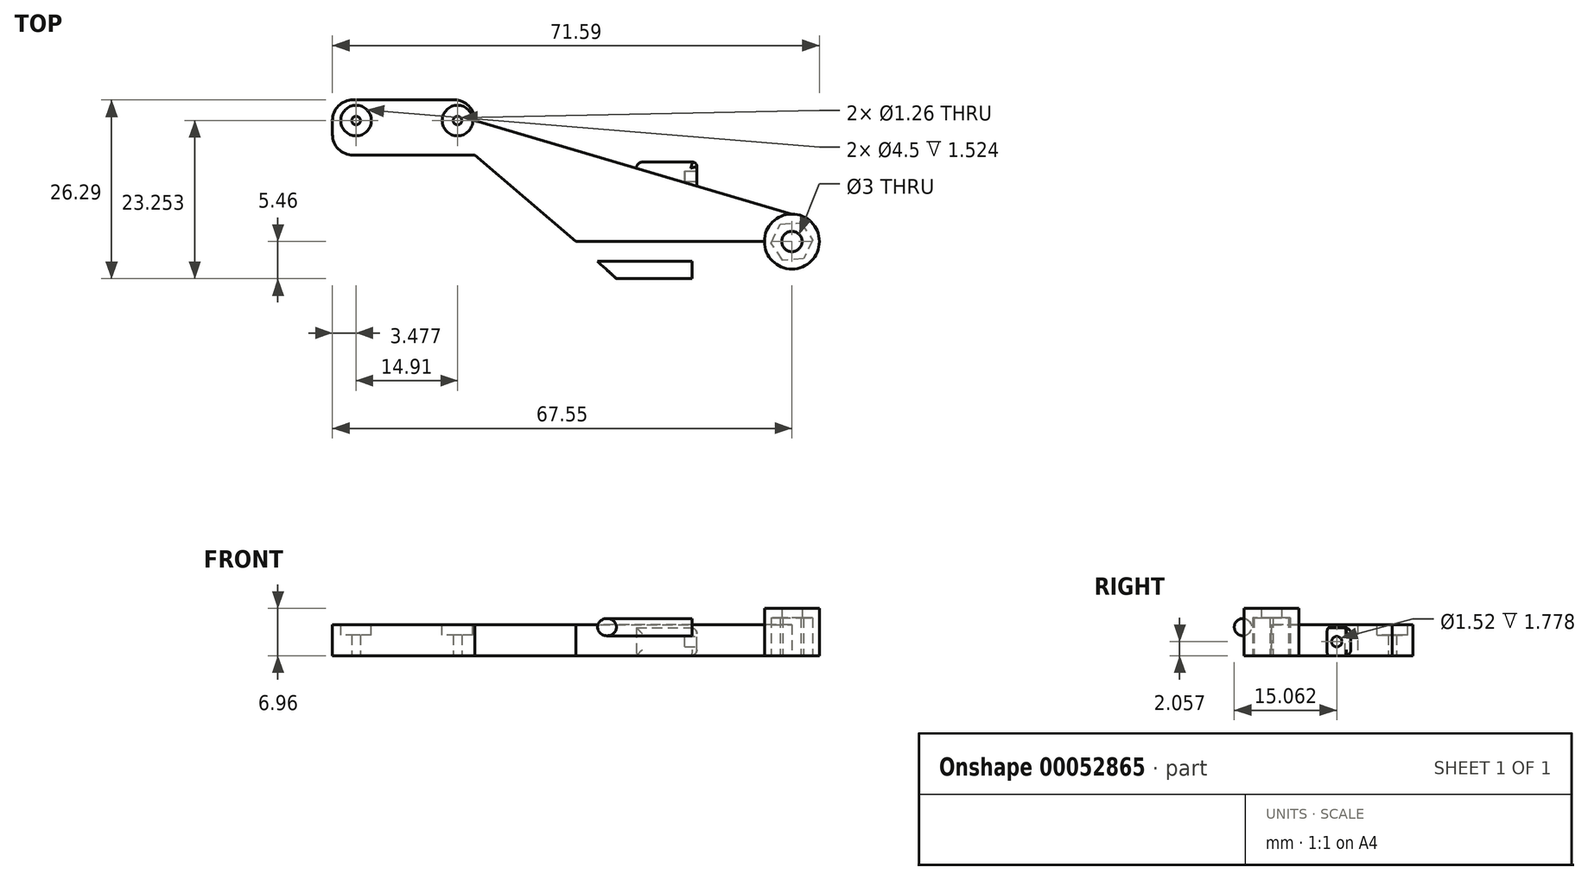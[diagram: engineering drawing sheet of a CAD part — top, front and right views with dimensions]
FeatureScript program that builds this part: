
annotation { "Feature Type Name" : "Feature", "Feature Type Description" : "" }
export const myFeature = defineFeature(function(context is Context, id is Id, definition is map)
    precondition{}
    {
        {
            var Q0;
            Q0=qCreatedBy(makeId("Top.planeOp"),FACE);
            var sketch = newSketch(context, id + "F0", { "sketchPlane" : qUnion([Q0])});
            skLineSegment(sketch, "E0", {"start": v(0, 0) * mm, "end": v(-31.75, 0) * mm});
            skLineSegment(sketch, "E1", {"start": v(-31.75, 0) * mm, "end": v(-46.62, 12.7) * mm});
            skLineSegment(sketch, "E2", {"start": v(-46.62, 12.7) * mm, "end": v(0, 0) * mm});
            skLineSegment(sketch, "E3", {"start": v(0, 0) * mm, "end": v(0, 4.04) * mm});
            skCircle(sketch, "E4", {"center": v(0, 0) * mm, "radius": 4.04 * mm});
            skLineSegment(sketch, "E5.bottom", {"start": v(-46.62, 12.7) * mm, "end": v(-64.5, 12.7) * mm});
            skLineSegment(sketch, "E5.top", {"start": v(-49.67, 20.83) * mm, "end": v(-64.5, 20.83) * mm});
            skLineSegment(sketch, "E5.left", {"start": v(-46.62, 12.7) * mm, "end": v(-46.62, 17.78) * mm});
            skLineSegment(sketch, "E5.right", {"start": v(-67.55, 15.75) * mm, "end": v(-67.55, 17.78) * mm});
            skCircle(sketch, "E6", {"center": v(-49.16, 17.8) * mm, "radius": 0.63 * mm});
            skCircle(sketch, "E7", {"center": v(-64.07, 17.8) * mm, "radius": 0.63 * mm});
            skPoint(sketch, "E8.visualSharp", {"position": v(-67.55, 20.83) * mm});
            skArc(sketch, "E8.filletArc", {"start": v(-64.5, 20.83) * mm, "mid": v(-66.66, 19.94) * mm, "end": v(-67.55, 17.78) * mm});
            skPoint(sketch, "E9.visualSharp", {"position": v(-67.55, 12.7) * mm});
            skArc(sketch, "E9.filletArc", {"start": v(-67.55, 15.75) * mm, "mid": v(-66.66, 13.6) * mm, "end": v(-64.5, 12.7) * mm});
            skPoint(sketch, "E10.visualSharp", {"position": v(-46.62, 20.83) * mm});
            skArc(sketch, "E10.filletArc", {"start": v(-46.62, 17.78) * mm, "mid": v(-47.52, 19.94) * mm, "end": v(-49.67, 20.83) * mm});
            skLineSegment(sketch, "E11", {"start": v(-46.62, 17.78) * mm, "end": v(0, 4.04) * mm});
            skLineSegment(sketch, "E12", {"start": v(-46.62, 12.7) * mm, "end": v(-49.67, 12.7) * mm});
            skLineSegment(sketch, "E13", {"start": v(-46.62, 12.7) * mm, "end": v(-44.3, 10.72) * mm});
            skLineSegment(sketch, "E14", {"start": v(-49.67, 12.7) * mm, "end": v(-44.3, 10.72) * mm});
            skCircle(sketch, "E15", {"center": v(0, 0) * mm, "radius": 1.5 * mm});
            skLineSegment(sketch, "E16", {"start": v(-44.3, 10.72) * mm, "end": v(-20.3, -9.78) * mm});
            skLineSegment(sketch, "E17", {"start": v(-21, -9.17) * mm, "end": v(-44.3, 10.72) * mm});
            skLineSegment(sketch, "E18", {"start": v(-31.75, 0) * mm, "end": v(-22.66, 0) * mm});
            skLineSegment(sketch, "E19", {"start": v(-22.66, 0) * mm, "end": v(-22.66, -4.18) * mm});
            skLineSegment(sketch, "E20", {"start": v(-22.66, 0) * mm, "end": v(-21.74, -2.29) * mm});
            skSolve(sketch);
        }
        {
            var Q0;
            Q0=makeQuery(id+"F0.imprint","IMPRINT",FACE,{"disambiguationData":[TD([[makeQuery(id+"F0.imprint","IMPRINT",EDGE,{"derivedFrom":sQuery(id+"F0.wireOp",EDGE,"E5.bottom")}),-1.0]])]});
            var Q1;
            Q1=makeQuery(id+"F0.imprint","IMPRINT",FACE,{"disambiguationData":[TD([[makeQuery(id+"F0.imprint","IMPRINT",EDGE,{"derivedFrom":sQuery(id+"F0.wireOp",EDGE,"E12")}),1.0]])]});
            var Q2;
            {var subQ0=sQuery(id+"F0.wireOp",EDGE,"E5.left");Q2=makeQuery(id+"F0.imprint","IMPRINT",FACE,{"disambiguationData":[TD([[makeQuery(id+"F0.imprint","IMPRINT",EDGE,{"derivedFrom":subQ0}),-1.0]])]});}
            var Q3;
            {var subQ5=sQuery(id+"F0.wireOp",EDGE,"E1");Q3=makeQuery(id+"F0.imprint","IMPRINT",FACE,{"disambiguationData":[TD([[makeQuery(id+"F0.imprint","IMPRINT",EDGE,{"derivedFrom":subQ5}),-1.0]])]});}
            var Q4;
            {var subQ0=sQuery(id+"F0.wireOp",EDGE,"E4");var subQ1=sQuery(id+"F0.wireOp",EDGE,"E2");var subQ2=makeQuery(id+"F0.imprint","INTERSECT",VERTEX,{"derivedFrom":[subQ1,subQ0]});Q4=makeQuery(id+"F0.imprint","IMPRINT",FACE,{"disambiguationData":[TD([[makeQuery(id+"F0.imprint","IMPRINT",EDGE,{"disambiguationData":[TD([[subQ2,-1.0]])],"derivedFrom":subQ1}),1.0]])]});}
            var Q5;
            {var subQ0=sQuery(id+"F0.wireOp",EDGE,"E4");var subQ1=sQuery(id+"F0.wireOp",EDGE,"E0");var subQ2=makeQuery(id+"F0.imprint","INTERSECT",VERTEX,{"derivedFrom":[subQ1,subQ0]});Q5=makeQuery(id+"F0.imprint","IMPRINT",FACE,{"disambiguationData":[TD([[makeQuery(id+"F0.imprint","IMPRINT",EDGE,{"disambiguationData":[TD([[subQ2,1.0]])],"derivedFrom":subQ1}),-1.0]])]});}
            var Q6;
            {var subQ0=sQuery(id+"F0.wireOp",EDGE,"E4");var subQ1=sQuery(id+"F0.wireOp",EDGE,"E0");var subQ2=makeQuery(id+"F0.imprint","INTERSECT",VERTEX,{"derivedFrom":[subQ1,subQ0]});Q6=makeQuery(id+"F0.imprint","IMPRINT",FACE,{"disambiguationData":[TD([[makeQuery(id+"F0.imprint","IMPRINT",EDGE,{"disambiguationData":[TD([[subQ2,1.0]])],"derivedFrom":subQ1}),1.0]])]});}
            var Q7;
            {var subQ0=sQuery(id+"F0.wireOp",EDGE,"E13");Q7=makeQuery(id+"F0.imprint","IMPRINT",FACE,{"disambiguationData":[TD([[makeQuery(id+"F0.imprint","IMPRINT",EDGE,{"derivedFrom":subQ0}),1.0]])]});}
            extrude(context, id + "F1", {"entities" : qUnion([Q0, Q1, Q2, Q3, Q4, Q5, Q6, Q7]), "depth" : 4.57 * mm});
        }
        {
            var Q0;
            {var subQ0=sQuery(id+"F0.wireOp",EDGE,"E4");var subQ1=sQuery(id+"F0.wireOp",EDGE,"E2");var subQ2=makeQuery(id+"F0.imprint","INTERSECT",VERTEX,{"derivedFrom":[subQ1,subQ0]});Q0=makeQuery(id+"F0.imprint","IMPRINT",FACE,{"disambiguationData":[TD([[makeQuery(id+"F0.imprint","IMPRINT",EDGE,{"disambiguationData":[TD([[subQ2,-1.0]])],"derivedFrom":subQ1}),1.0]])]});}
            var Q1;
            {var subQ0=sQuery(id+"F0.wireOp",EDGE,"E4");var subQ1=sQuery(id+"F0.wireOp",EDGE,"E0");var subQ2=makeQuery(id+"F0.imprint","INTERSECT",VERTEX,{"derivedFrom":[subQ1,subQ0]});Q1=makeQuery(id+"F0.imprint","IMPRINT",FACE,{"disambiguationData":[TD([[makeQuery(id+"F0.imprint","IMPRINT",EDGE,{"disambiguationData":[TD([[subQ2,1.0]])],"derivedFrom":subQ1}),1.0]])]});}
            var Q2;
            {var subQ0=sQuery(id+"F0.wireOp",EDGE,"E4");var subQ1=sQuery(id+"F0.wireOp",EDGE,"E0");var subQ2=makeQuery(id+"F0.imprint","INTERSECT",VERTEX,{"derivedFrom":[subQ1,subQ0]});Q2=makeQuery(id+"F0.imprint","IMPRINT",FACE,{"disambiguationData":[TD([[makeQuery(id+"F0.imprint","IMPRINT",EDGE,{"disambiguationData":[TD([[subQ2,1.0]])],"derivedFrom":subQ1}),-1.0]])]});}
            extrude(context, id + "F2", {"entities" : qUnion([Q0, Q1, Q2]), "operationType" : NewBodyOperationType.ADD, "depth" : 6.96 * mm});
        }
        {
            var Q0;
            Q0=makeQuery(id+"F1.opExtrude","CAP_FACE",FACE,{"disambiguationData":[OSD([sQuery(id+"F0.wireOp",EDGE,"E0"),sQuery(id+"F0.wireOp",EDGE,"E1"),sQuery(id+"F0.wireOp",EDGE,"E4"),sQuery(id+"F0.wireOp",EDGE,"E5.bottom"),sQuery(id+"F0.wireOp",EDGE,"E5.top"),sQuery(id+"F0.wireOp",EDGE,"E5.right"),sQuery(id+"F0.wireOp",EDGE,"E6"),sQuery(id+"F0.wireOp",EDGE,"E7"),sQuery(id+"F0.wireOp",EDGE,"E8.filletArc"),sQuery(id+"F0.wireOp",EDGE,"E9.filletArc"),sQuery(id+"F0.wireOp",EDGE,"E10.filletArc"),sQuery(id+"F0.wireOp",EDGE,"E11"),sQuery(id+"F0.wireOp",EDGE,"E14"),sQuery(id+"F0.wireOp",EDGE,"E15")])],"isStart":false});
            var sketch = newSketch(context, id + "F3", { "sketchPlane" : qUnion([Q0])});
            skCircle(sketch, "E21", {"center": v(-64.07, 17.8) * mm, "radius": 2.25 * mm});
            skCircle(sketch, "E22", {"center": v(-49.16, 17.8) * mm, "radius": 1.35 * mm});
            skCircle(sketch, "E23", {"center": v(-49.16, 17.8) * mm, "radius": 2.25 * mm});
            skSolve(sketch);
        }
        {
            var Q0;
            Q0=makeQuery(id+"F3.imprint","IMPRINT",FACE,{"disambiguationData":[TD([[makeQuery(id+"F3.imprint","IMPRINT",EDGE,{"derivedFrom":sQuery(id+"F3.wireOp",EDGE,"E21")}),1.0]])]});
            var Q1;
            Q1=makeQuery(id+"F3.imprint","IMPRINT",FACE,{"disambiguationData":[TD([[makeQuery(id+"F3.imprint","IMPRINT",EDGE,{"derivedFrom":sQuery(id+"F3.wireOp",EDGE,"E22")}),-1.0]])]});
            var Q2;
            Q2=makeQuery(id+"F3.imprint","IMPRINT",FACE,{"disambiguationData":[TD([[makeQuery(id+"F3.imprint","IMPRINT",EDGE,{"derivedFrom":sQuery(id+"F3.wireOp",EDGE,"E22")}),1.0]])]});
            extrude(context, id + "F4", {"entities" : qUnion([Q0, Q1, Q2]), "operationType" : NewBodyOperationType.REMOVE, "oppositeDirection" : true, "depth" : 1.52 * mm});
        }
        {
            var Q0;
            Q0=qCreatedBy(makeId("Top.planeOp"),FACE);
            var sketch = newSketch(context, id + "F5", { "sketchPlane" : qUnion([Q0])});
            skLineSegment(sketch, "E24", {"start": v(0, 0) * mm, "end": v(-14.7, 0) * mm});
            skLineSegment(sketch, "E25", {"start": v(-14.7, 0) * mm, "end": v(-14.7, -8.38) * mm});
            skLineSegment(sketch, "E26", {"start": v(-14.7, 0) * mm, "end": v(-31.75, 0) * mm});
            skLineSegment(sketch, "E27", {"start": v(-14.7, -8.38) * mm, "end": v(-22.62, -8.38) * mm});
            skLineSegment(sketch, "E28", {"start": v(-22.62, -8.38) * mm, "end": v(-31.75, 0) * mm});
            skLineSegment(sketch, "E29", {"start": v(-14.6, 11.68) * mm, "end": v(-22.86, 11.68) * mm});
            skLineSegment(sketch, "E30", {"start": v(-22.86, 11.68) * mm, "end": v(-22.86, 4.7) * mm});
            skLineSegment(sketch, "E31", {"start": v(-22.86, 4.7) * mm, "end": v(-13.97, 4.7) * mm});
            skLineSegment(sketch, "E32", {"start": v(-13.97, 4.7) * mm, "end": v(-13.97, 11.05) * mm});
            skPoint(sketch, "E33.visualSharp", {"position": v(-13.97, 11.68) * mm});
            skArc(sketch, "E33.filletArc", {"start": v(-13.97, 11.05) * mm, "mid": v(-14.16, 11.5) * mm, "end": v(-14.6, 11.68) * mm});
            skSolve(sketch);
        }
        {
            var Q0;
            Q0=makeQuery(id+"F5.imprint","IMPRINT",FACE,{"disambiguationData":[TD([[makeQuery(id+"F5.imprint","IMPRINT",EDGE,{"derivedFrom":sQuery(id+"F5.wireOp",EDGE,"E29")}),1.0]])]});
            extrude(context, id + "F6", {"entities" : qUnion([Q0]), "operationType" : NewBodyOperationType.ADD, "depth" : 4.11 * mm});
        }
        {
            var Q0;
            Q0=makeQuery(id+"F5.imprint","IMPRINT",FACE,{"disambiguationData":[TD([[makeQuery(id+"F5.imprint","IMPRINT",EDGE,{"derivedFrom":sQuery(id+"F5.wireOp",EDGE,"E25")}),-1.0]])]});
            extrude(context, id + "F7", {"entities" : qUnion([Q0]), "operationType" : NewBodyOperationType.ADD, "depth" : 8.38 * mm});
        }
        {
            var Q0;
            Q0=makeQuery(id+"F7.opExtrude","CAP_EDGE",EDGE,{"disambiguationData":[OSD([sQuery(id+"F5.wireOp",EDGE,"E26")])],"isStart":false});
            var Q1;
            Q1=makeQuery(id+"F7.opExtrude","CAP_EDGE",EDGE,{"disambiguationData":[OSD([sQuery(id+"F5.wireOp",EDGE,"E27")])],"isStart":false});
            var Q2;
            Q2=makeQuery(id+"F7.opExtrude","CAP_EDGE",EDGE,{"disambiguationData":[OSD([sQuery(id+"F5.wireOp",EDGE,"E27")])],"isStart":true});
            fillet(context, id + "F8", {"entities" : qUnion([Q0, Q1, Q2]), "radius" : 3.8 * mm, "tangentPropagation" : true, "allowEdgeOverflow" : false});
        }
        {
            var Q0;
            Q0=makeQuery(id+"F7.opExtrude","SWEPT_FACE",FACE,{"disambiguationData":[OSD([sQuery(id+"F5.wireOp",EDGE,"E25")])]});
            var sketch = newSketch(context, id + "F9", { "sketchPlane" : qUnion([Q0])});
            skLineSegment(sketch, "E34", {"start": v(-4.2, 8.38) * mm, "end": v(-4.2, 0) * mm});
            skCircle(sketch, "E35", {"center": v(-4.2, 4.2) * mm, "radius": 1.27 * mm});
            skSolve(sketch);
        }
        {
            var Q0;
            {var subQ0=sQuery(id+"F9.wireOp",EDGE,"E35");var subQ1=sQuery(id+"F9.wireOp",EDGE,"E34");var subQ2=makeQuery(id+"F9.imprint","INTERSECT",VERTEX,{"disambiguationData":[OD(0.0)],"derivedFrom":[subQ1,subQ0]});Q0=makeQuery(id+"F9.imprint","IMPRINT",FACE,{"disambiguationData":[TD([[makeQuery(id+"F9.imprint","IMPRINT",EDGE,{"disambiguationData":[TD([[subQ2,-1.0]])],"derivedFrom":subQ1}),-1.0]])]});}
            var Q1;
            {var subQ0=sQuery(id+"F9.wireOp",EDGE,"E35");var subQ1=sQuery(id+"F9.wireOp",EDGE,"E34");var subQ2=makeQuery(id+"F9.imprint","INTERSECT",VERTEX,{"disambiguationData":[OD(0.0)],"derivedFrom":[subQ1,subQ0]});Q1=makeQuery(id+"F9.imprint","IMPRINT",FACE,{"disambiguationData":[TD([[makeQuery(id+"F9.imprint","IMPRINT",EDGE,{"disambiguationData":[TD([[subQ2,-1.0]])],"derivedFrom":subQ1}),1.0]])]});}
            var Q2;
            Q2 = qSketchRegion(id + "F12", true);
            extrude(context, id + "F10", {"entities" : qUnion([Q0, Q1, Q2]), "operationType" : NewBodyOperationType.REMOVE, "oppositeDirection" : true, "depth" : 25.4 * mm});
        }
        {
            var Q0;
            Q0=makeQuery(id+"F7.opExtrude","SWEPT_FACE",FACE,{"disambiguationData":[OSD([sQuery(id+"F5.wireOp",EDGE,"E25")])]});
            cPlane(context, id + "F11", {"entities" : qUnion([Q0]), "cplaneType" : CPlaneType.OFFSET, "offset" : 2.3 * mm, "oppositeDirection" : true, "width" : 152.4 * mm, "height" : 152.4 * mm});
        }
        {
            var Q0;
            Q0=qCreatedBy(id+"F11.planeOp",FACE);
            var sketch = newSketch(context, id + "F12", { "sketchPlane" : qUnion([Q0])});
            skCircle(sketch, "E36", {"center": v(-4.19, 4.19) * mm, "radius": 2.8 * mm});
            skCircle(sketch, "E37", {"center": v(-4.19, 4.19) * mm, "radius": 1.27 * mm});
            skSolve(sketch);
        }
        {
            var Q0;
            Q0 = qSketchRegion(id + "F12", true);
            extrude(context, id + "F13", {"entities" : qUnion([Q0]), "operationType" : NewBodyOperationType.REMOVE, "oppositeDirection" : true, "depth" : 25.4 * mm});
        }
        {
            var Q0;
            Q0=makeQuery(id+"F6.opExtrude","SWEPT_EDGE",EDGE,{"disambiguationData":[OSD([sQuery(id+"F5.wireOp",EDGE,"E29"),sQuery(id+"F5.wireOp",EDGE,"E30")])]});
            var Q1;
            Q1=makeQuery(id+"F6.opExtrude","CAP_EDGE",EDGE,{"disambiguationData":[OSD([sQuery(id+"F5.wireOp",EDGE,"E29")])],"isStart":false});
            var Q2;
            Q2=makeQuery(id+"F6.opExtrude","CAP_EDGE",EDGE,{"disambiguationData":[OSD([sQuery(id+"F5.wireOp",EDGE,"E29")])],"isStart":true});
            var Q3;
            Q3=makeQuery(id+"F6.opExtrude","SWEPT_EDGE",EDGE,{"disambiguationData":[OSD([sQuery(id+"F5.wireOp",EDGE,"E29"),sQuery(id+"F5.wireOp",EDGE,"E33.filletArc")])]});
            var Q4;
            Q4=makeQuery(id+"F6.opExtrude","SWEPT_EDGE",EDGE,{"disambiguationData":[OSD([sQuery(id+"F5.wireOp",EDGE,"E32"),sQuery(id+"F5.wireOp",EDGE,"E33.filletArc")])]});
            fillet(context, id + "F14", {"entities" : qUnion([Q0, Q1, Q2, Q3, Q4]), "radius" : 0.89 * mm, "tangentPropagation" : true, "allowEdgeOverflow" : false});
        }
        {
            var Q0;
            Q0=makeQuery(id+"F6.opExtrude","SWEPT_FACE",FACE,{"disambiguationData":[OSD([sQuery(id+"F5.wireOp",EDGE,"E32")])]});
            var sketch = newSketch(context, id + "F15", { "sketchPlane" : qUnion([Q0])});
            skPoint(sketch, "E38.endSnap0", {"position": v(9.6, 3.23) * mm});
            skCircle(sketch, "E39", {"center": v(9.6, 2.06) * mm, "radius": 0.76 * mm});
            skSolve(sketch);
        }
        {
            var Q0;
            Q0 = qSketchRegion(id + "F15", true);
            extrude(context, id + "F16", {"entities" : qUnion([Q0]), "operationType" : NewBodyOperationType.REMOVE, "oppositeDirection" : true, "depth" : 1.78 * mm});
        }
        {
            var Q0;
            {var subQ0=sQuery(id+"F0.wireOp",EDGE,"E4");var subQ1=sQuery(id+"F0.wireOp",EDGE,"E0");var subQ2=makeQuery(id+"F0.imprint","INTERSECT",VERTEX,{"derivedFrom":[subQ1,subQ0]});Q0=makeQuery(id+"F0.imprint","IMPRINT",FACE,{"disambiguationData":[TD([[makeQuery(id+"F0.imprint","IMPRINT",EDGE,{"disambiguationData":[TD([[subQ2,1.0]])],"derivedFrom":subQ1}),1.0]])]});}
            var sketch = newSketch(context, id + "F17", { "sketchPlane" : qUnion([Q0])});
            skCircle(sketch, "E40", {"center": v(0, 0) * mm, "radius": 1.5 * mm});
            skLineSegment(sketch, "E41.1", {"start": v(1.72, -2.55) * mm, "end": v(-1.35, -2.76) * mm});
            skLineSegment(sketch, "E41.2", {"start": v(-1.35, -2.76) * mm, "end": v(-3.07, -0.21) * mm});
            skLineSegment(sketch, "E41.3", {"start": v(-3.07, -0.21) * mm, "end": v(-1.72, 2.55) * mm});
            skLineSegment(sketch, "E41.4", {"start": v(-1.72, 2.55) * mm, "end": v(1.35, 2.76) * mm});
            skLineSegment(sketch, "E41.5", {"start": v(1.35, 2.76) * mm, "end": v(3.07, 0.21) * mm});
            skLineSegment(sketch, "E42", {"start": v(3.07, 0.21) * mm, "end": v(1.72, -2.55) * mm});
            skLineSegment(sketch, "E43", {"start": v(0, 0) * mm, "end": v(1.35, 2.76) * mm});
            skLineSegment(sketch, "E44", {"start": v(0, 0) * mm, "end": v(-1.35, -2.76) * mm});
            skSolve(sketch);
        }
        {
            var Q0;
            Q0 = qSketchRegion(id + "F17", true);
            extrude(context, id + "F18", {"entities" : qUnion([Q0]), "operationType" : NewBodyOperationType.REMOVE, "depth" : 5.6 * mm});
        }
    });
